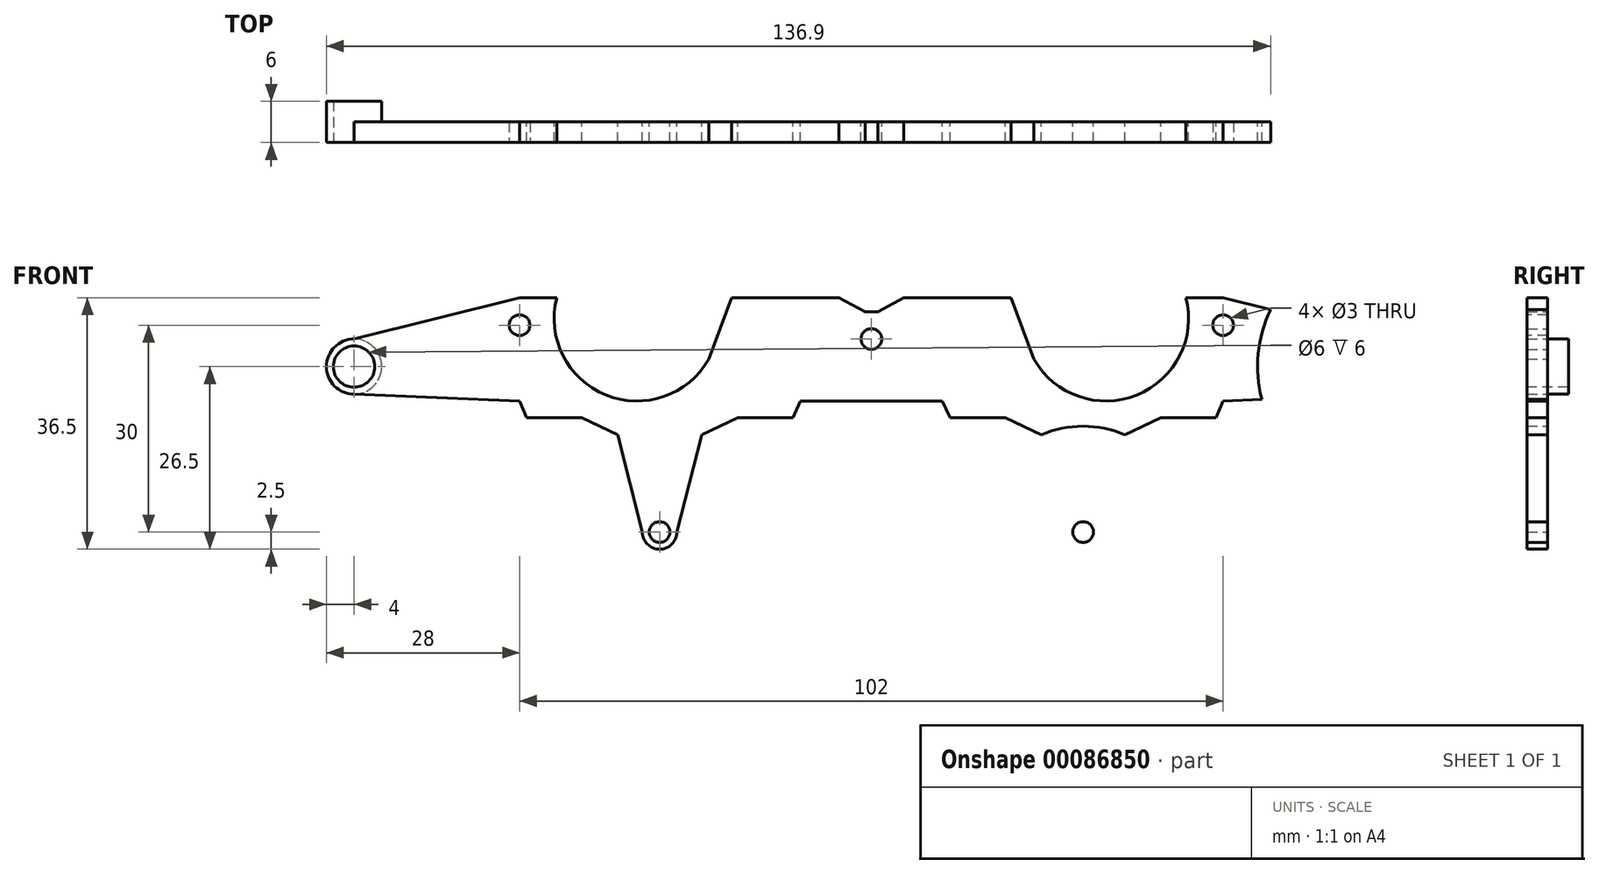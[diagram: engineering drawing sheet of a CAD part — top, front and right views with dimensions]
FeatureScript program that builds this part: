
annotation { "Feature Type Name" : "Feature", "Feature Type Description" : "" }
export const myFeature = defineFeature(function(context is Context, id is Id, definition is map)
    precondition{}
    {
        {
            var Q0;
            Q0=qCreatedBy(makeId("Front.planeOp"),FACE);
            var sketch = newSketch(context, id + "F0", { "sketchPlane" : qUnion([Q0])});
            skCircle(sketch, "E0", {"center": v(-75, 14) * mm, "radius": 16 * mm, "construction": true});
            skCircle(sketch, "E1", {"center": v(-46, -16) * mm, "radius": 9 * mm, "construction": true});
            skCircle(sketch, "E2", {"center": v(-15.4, -16) * mm, "radius": 9 * mm, "construction": true});
            skCircle(sketch, "E3", {"center": v(-34, 21) * mm, "radius": 9 * mm, "construction": true});
            skLineSegment(sketch, "E4", {"start": v(-75, 14) * mm, "end": v(75, 14) * mm, "construction": true});
            skLineSegment(sketch, "E5", {"start": v(-30.7, 14) * mm, "end": v(-30.7, -10) * mm, "construction": true});
            skArc(sketch, "E6", {"start": v(-75, 18) * mm, "mid": v(-79, 14) * mm, "end": v(-75, 10) * mm});
            skLineSegment(sketch, "E7", {"start": v(-51, 9) * mm, "end": v(-51, 24) * mm, "construction": true});
            skLineSegment(sketch, "E8", {"start": v(-75, 18) * mm, "end": v(-51, 24) * mm});
            skLineSegment(sketch, "E9", {"start": v(-51, 9) * mm, "end": v(-75, 10) * mm});
            skArc(sketch, "E10", {"start": v(-33.2, -10) * mm, "mid": v(-30.7, -12.5) * mm, "end": v(-28.2, -10) * mm});
            skLineSegment(sketch, "E11", {"start": v(-34, 21) * mm, "end": v(0, 18) * mm, "construction": true});
            skLineSegment(sketch, "E12", {"start": v(-51, 24) * mm, "end": v(-45.62, 24) * mm});
            skArc(sketch, "E13", {"start": v(-45.62, 24) * mm, "mid": v(-38.5, 9.88) * mm, "end": v(-23.57, 15.06) * mm});
            skLineSegment(sketch, "E14", {"start": v(-46, -16) * mm, "end": v(-30.7, -10) * mm, "construction": true});
            skLineSegment(sketch, "E15", {"start": v(-15.4, -16) * mm, "end": v(-30.7, -10) * mm, "construction": true});
            skLineSegment(sketch, "E16", {"start": v(-4.7, 24) * mm, "end": v(0, 24) * mm});
            skLineSegment(sketch, "E17", {"start": v(0, 18) * mm, "end": v(-29.94, 34.4) * mm, "construction": true});
            skCircle(sketch, "E18", {"center": v(-75, 14) * mm, "radius": 4 * mm});
            skCircle(sketch, "E19", {"center": v(-29.94, 34.4) * mm, "radius": 9 * mm, "construction": true});
            skArc(sketch, "E20", {"start": v(-56.6, 9.23) * mm, "mid": v(-56.1, 15.87) * mm, "end": v(-57.9, 22.28) * mm});
            skLineSegment(sketch, "E21", {"start": v(0, 24) * mm, "end": v(0, 24) * mm});
            skCircle(sketch, "E22", {"center": v(-30.7, -10) * mm, "radius": 1.5 * mm});
            skLineSegment(sketch, "E23", {"start": v(-24.6, 4.1) * mm, "end": v(-19.4, 6.6) * mm});
            skLineSegment(sketch, "E24", {"start": v(-36.8, 4.1) * mm, "end": v(-42, 6.6) * mm});
            skArc(sketch, "E25", {"start": v(-24.6, 4.1) * mm, "mid": v(-30.7, 5.35) * mm, "end": v(-36.8, 4.1) * mm});
            skLineSegment(sketch, "E26", {"start": v(-23.57, 15.06) * mm, "end": v(0, 12.98) * mm});
            skCircle(sketch, "E27", {"center": v(-75, 14) * mm, "radius": 3 * mm});
            skLineSegment(sketch, "E28", {"start": v(-28.2, -10) * mm, "end": v(-24.6, 4.1) * mm});
            skLineSegment(sketch, "E29", {"start": v(-36.8, 4.1) * mm, "end": v(-33.2, -10) * mm});
            skLineSegment(sketch, "E30", {"start": v(-11.4, 6.6) * mm, "end": v(-19.4, 6.6) * mm});
            skLineSegment(sketch, "E31", {"start": v(-42, 6.6) * mm, "end": v(-50, 6.6) * mm});
            skLineSegment(sketch, "E32", {"start": v(-50, 6.6) * mm, "end": v(-51, 9) * mm});
            skLineSegment(sketch, "E33", {"start": v(-4.7, 24) * mm, "end": v(-0.92, 21.92) * mm});
            skPoint(sketch, "E34", {"position": v(-46, 6.6) * mm});
            skPoint(sketch, "E35", {"position": v(-15.4, 6.6) * mm});
            skLineSegment(sketch, "E36", {"start": v(-11.4, 6.6) * mm, "end": v(-10.28, 9) * mm});
            skLineSegment(sketch, "E37", {"start": v(-4.7, 24) * mm, "end": v(-20.26, 24) * mm});
            skArc(sketch, "E38", {"start": v(-22.04, 30.08) * mm, "mid": v(-24.05, 25.3) * mm, "end": v(-25.04, 20.2) * mm, "construction": true});
            skCircle(sketch, "E39.MirrorC", {"center": v(30.7, -10) * mm, "radius": 1.5 * mm});
            skLineSegment(sketch, "E40.MirrorCS", {"start": v(4.7, 24) * mm, "end": v(0, 24) * mm});
            skLineSegment(sketch, "E41.MirrorCS", {"start": v(4.7, 24) * mm, "end": v(0.92, 21.92) * mm});
            skLineSegment(sketch, "E42.MirrorCS", {"start": v(50, 6.6) * mm, "end": v(51, 9) * mm});
            skArc(sketch, "E43.MirrorCS", {"start": v(33.2, -10) * mm, "mid": v(30.7, -12.5) * mm, "end": v(28.2, -10) * mm});
            skLineSegment(sketch, "E44.MirrorCS", {"start": v(11.4, 6.6) * mm, "end": v(10.28, 9) * mm});
            skLineSegment(sketch, "E45.MirrorCS", {"start": v(28.2, -10) * mm, "end": v(24.6, 4.1) * mm});
            skLineSegment(sketch, "E46.MirrorCS", {"start": v(36.8, 4.1) * mm, "end": v(33.2, -10) * mm});
            skLineSegment(sketch, "E47.MirrorCS", {"start": v(42, 6.6) * mm, "end": v(50, 6.6) * mm});
            skArc(sketch, "E48.MirrorCS", {"start": v(22.04, 30.08) * mm, "mid": v(24.05, 25.3) * mm, "end": v(25.04, 20.2) * mm, "construction": true});
            skLineSegment(sketch, "E49.MirrorCS", {"start": v(19.4, 6.6) * mm, "end": v(11.4, 6.6) * mm});
            skLineSegment(sketch, "E50.MirrorCS", {"start": v(24.6, 4.1) * mm, "end": v(19.4, 6.6) * mm});
            skCircle(sketch, "E51.MirrorC", {"center": v(75, 14) * mm, "radius": 16 * mm, "construction": true});
            skCircle(sketch, "E52.MirrorC", {"center": v(29.94, 34.4) * mm, "radius": 9 * mm, "construction": true});
            skCircle(sketch, "E53.MirrorC", {"center": v(15.4, -16) * mm, "radius": 9 * mm, "construction": true});
            skLineSegment(sketch, "E54.MirrorCS", {"start": v(15.4, -16) * mm, "end": v(30.7, -10) * mm, "construction": true});
            skLineSegment(sketch, "E55.MirrorCS", {"start": v(36.8, 4.1) * mm, "end": v(42, 6.6) * mm});
            skLineSegment(sketch, "E56.MirrorCS", {"start": v(30.7, 14) * mm, "end": v(30.7, -10) * mm, "construction": true});
            skArc(sketch, "E57.MirrorCS", {"start": v(56.6, 9.23) * mm, "mid": v(56.1, 15.87) * mm, "end": v(57.9, 22.28) * mm});
            skArc(sketch, "E58.MirrorCS", {"start": v(45.62, 24) * mm, "mid": v(38.5, 9.88) * mm, "end": v(23.57, 15.06) * mm});
            skCircle(sketch, "E59.MirrorC", {"center": v(46, -16) * mm, "radius": 9 * mm, "construction": true});
            skCircle(sketch, "E60.MirrorC", {"center": v(75, 14) * mm, "radius": 1.5 * mm});
            skArc(sketch, "E61.MirrorCS", {"start": v(24.6, 4.1) * mm, "mid": v(30.7, 5.35) * mm, "end": v(36.8, 4.1) * mm});
            skLineSegment(sketch, "E62.MirrorCS", {"start": v(51, 9) * mm, "end": v(51, 24) * mm, "construction": true});
            skPoint(sketch, "E63.MirrorP", {"position": v(46, 6.6) * mm});
            skCircle(sketch, "E64.MirrorC", {"center": v(34, 21) * mm, "radius": 9 * mm, "construction": true});
            skPoint(sketch, "E65.MirrorP", {"position": v(15.4, 6.6) * mm});
            skLineSegment(sketch, "E66.MirrorCS", {"start": v(0, 18) * mm, "end": v(29.94, 34.4) * mm, "construction": true});
            skLineSegment(sketch, "E67.MirrorCS", {"start": v(51, 24) * mm, "end": v(45.62, 24) * mm});
            skLineSegment(sketch, "E68.MirrorCS", {"start": v(23.57, 15.06) * mm, "end": v(0, 12.98) * mm});
            skLineSegment(sketch, "E69.MirrorCS", {"start": v(4.7, 24) * mm, "end": v(20.26, 24) * mm});
            skLineSegment(sketch, "E70.MirrorCS", {"start": v(51, 9) * mm, "end": v(56.6, 9.23) * mm});
            skLineSegment(sketch, "E71.MirrorCS", {"start": v(34, 21) * mm, "end": v(0, 18) * mm, "construction": true});
            skLineSegment(sketch, "E72.MirrorCS", {"start": v(46, -16) * mm, "end": v(30.7, -10) * mm, "construction": true});
            skLineSegment(sketch, "E73", {"start": v(-10.28, 9) * mm, "end": v(10.28, 9) * mm});
            skCircle(sketch, "E74", {"center": v(0, 18) * mm, "radius": 1.5 * mm});
            skLineSegment(sketch, "E75", {"start": v(51, 24) * mm, "end": v(57.9, 22.28) * mm});
            skLineSegment(sketch, "E76", {"start": v(57.9, 22.28) * mm, "end": v(73.57, 21.87) * mm});
            skLineSegment(sketch, "E77", {"start": v(73.57, 21.87) * mm, "end": v(83, 21.87) * mm});
            skLineSegment(sketch, "E78", {"start": v(56.6, 9.23) * mm, "end": v(83, 9.23) * mm});
            skLineSegment(sketch, "E79", {"start": v(83, 9.23) * mm, "end": v(83, 21.87) * mm});
            skLineSegment(sketch, "E80", {"start": v(-0.92, 21.92) * mm, "end": v(0.92, 21.92) * mm});
            skLineSegment(sketch, "E81", {"start": v(-20.26, 24) * mm, "end": v(-23.57, 15.06) * mm});
            skLineSegment(sketch, "E82", {"start": v(20.26, 24) * mm, "end": v(23.57, 15.06) * mm});
            skSolve(sketch);
        }
        {
            var Q0;
            {var subQ3=sQuery(id+"F0.wireOp",EDGE,"E20");Q0=makeQuery(id+"F0.imprint","IMPRINT",FACE,{"disambiguationData":[TD([[makeQuery(id+"F0.imprint","IMPRINT",EDGE,{"derivedFrom":subQ3}),1.0]])]});}
            var Q1;
            {var subQ4=sQuery(id+"F0.wireOp",EDGE,"E12");Q1=makeQuery(id+"F0.imprint","IMPRINT",FACE,{"disambiguationData":[TD([[makeQuery(id+"F0.imprint","IMPRINT",EDGE,{"derivedFrom":subQ4}),-1.0]])]});}
            var Q2;
            Q2=makeQuery(id+"F0.imprint","IMPRINT",FACE,{"disambiguationData":[TD([[makeQuery(id+"F0.imprint","IMPRINT",EDGE,{"derivedFrom":sQuery(id+"F0.wireOp",EDGE,"E26")}),1.0]])]});
            var Q3;
            {var subQ1=sQuery(id+"F0.wireOp",EDGE,"E57.MirrorCS");Q3=makeQuery(id+"F0.imprint","IMPRINT",FACE,{"disambiguationData":[TD([[makeQuery(id+"F0.imprint","IMPRINT",EDGE,{"derivedFrom":subQ1}),-1.0]])]});}
            var Q4;
            Q4=makeQuery(id+"F0.imprint","IMPRINT",FACE,{"disambiguationData":[TD([[makeQuery(id+"F0.imprint","IMPRINT",EDGE,{"derivedFrom":sQuery(id+"F0.wireOp",EDGE,"E39.MirrorC")}),1.0]])]});
            var Q5;
            Q5=makeQuery(id+"F0.imprint","IMPRINT",FACE,{"disambiguationData":[TD([[makeQuery(id+"F0.imprint","IMPRINT",EDGE,{"derivedFrom":sQuery(id+"F0.wireOp",EDGE,"E10")}),1.0]])]});
            extrude(context, id + "F1", {"entities" : qUnion([Q0, Q1, Q2, Q3, Q4, Q5]), "depth" : 3 * mm});
        }
        {
            var Q0;
            Q0=makeQuery(id+"F0.imprint","IMPRINT",FACE,{"disambiguationData":[TD([[makeQuery(id+"F0.imprint","IMPRINT",EDGE,{"derivedFrom":sQuery(id+"F0.wireOp",EDGE,"E27")}),-1.0]])]});
            extrude(context, id + "F2", {"entities" : qUnion([Q0]), "operationType" : NewBodyOperationType.ADD, "oppositeDirection" : true, "depth" : (2 * 2.5 + 1) * mm, "symmetric" : true});
        }
        {
            var Q0;
            {var subQ0=sQuery(id+"F0.wireOp",EDGE,"E18");Q0=makeQuery(id+"F2.boolean.opBoolean","MERGE",FACE,{"derivedFrom":[makeQuery(id+"F1.opExtrude","CAP_FACE",FACE,{"disambiguationData":[OSD([sQuery(id+"F0.wireOp",EDGE,"E8"),sQuery(id+"F0.wireOp",EDGE,"E9"),sQuery(id+"F0.wireOp",EDGE,"E10"),sQuery(id+"F0.wireOp",EDGE,"E12"),sQuery(id+"F0.wireOp",EDGE,"E13"),subQ0,sQuery(id+"F0.wireOp",EDGE,"E22"),sQuery(id+"F0.wireOp",EDGE,"E23"),sQuery(id+"F0.wireOp",EDGE,"E24"),sQuery(id+"F0.wireOp",EDGE,"E28"),sQuery(id+"F0.wireOp",EDGE,"E29"),sQuery(id+"F0.wireOp",EDGE,"E30"),sQuery(id+"F0.wireOp",EDGE,"E31"),sQuery(id+"F0.wireOp",EDGE,"E32"),sQuery(id+"F0.wireOp",EDGE,"E33"),sQuery(id+"F0.wireOp",EDGE,"E36"),sQuery(id+"F0.wireOp",EDGE,"E37"),sQuery(id+"F0.wireOp",EDGE,"E39.MirrorC"),sQuery(id+"F0.wireOp",EDGE,"E41.MirrorCS"),sQuery(id+"F0.wireOp",EDGE,"E42.MirrorCS"),sQuery(id+"F0.wireOp",EDGE,"E43.MirrorCS"),sQuery(id+"F0.wireOp",EDGE,"E44.MirrorCS"),sQuery(id+"F0.wireOp",EDGE,"E45.MirrorCS"),sQuery(id+"F0.wireOp",EDGE,"E46.MirrorCS"),sQuery(id+"F0.wireOp",EDGE,"E47.MirrorCS"),sQuery(id+"F0.wireOp",EDGE,"E49.MirrorCS"),sQuery(id+"F0.wireOp",EDGE,"E50.MirrorCS"),sQuery(id+"F0.wireOp",EDGE,"E55.MirrorCS"),sQuery(id+"F0.wireOp",EDGE,"E58.MirrorCS"),sQuery(id+"F0.wireOp",EDGE,"E60.MirrorC"),sQuery(id+"F0.wireOp",EDGE,"E67.MirrorCS"),sQuery(id+"F0.wireOp",EDGE,"E69.MirrorCS"),sQuery(id+"F0.wireOp",EDGE,"E70.MirrorCS"),sQuery(id+"F0.wireOp",EDGE,"E73"),sQuery(id+"F0.wireOp",EDGE,"E74"),sQuery(id+"F0.wireOp",EDGE,"E75"),sQuery(id+"F0.wireOp",EDGE,"E76"),sQuery(id+"F0.wireOp",EDGE,"E77"),sQuery(id+"F0.wireOp",EDGE,"E78"),sQuery(id+"F0.wireOp",EDGE,"E79"),sQuery(id+"F0.wireOp",EDGE,"E80"),sQuery(id+"F0.wireOp",EDGE,"E81"),sQuery(id+"F0.wireOp",EDGE,"E82")])],"isStart":false}),makeQuery(id+"F2.opExtrude","CAP_FACE",FACE,{"disambiguationData":[OSD([subQ0,sQuery(id+"F0.wireOp",EDGE,"E27")])],"isStart":true})]});}
            var sketch = newSketch(context, id + "F3", { "sketchPlane" : qUnion([Q0])});
            skLineSegment(sketch, "E83", {"start": v(-51, 24) * mm, "end": v(-51, 20) * mm, "construction": true});
            skLineSegment(sketch, "E84", {"start": v(51, 24) * mm, "end": v(51, 20) * mm, "construction": true});
            skSolve(sketch);
        }
        {
            var Q0;
            Q0=sQuery(id+"F3.wireOp",VERTEX,"E83.end");
            var Q1;
            Q1=sQuery(id+"F3.wireOp",VERTEX,"E84.end");
            var Q2;
            Q2=makeQuery(id+"F1.opExtrude","SWEPT_BODY",BODY,{"disambiguationData":[OSD([sQuery(id+"F0.wireOp",EDGE,"E8"),sQuery(id+"F0.wireOp",EDGE,"E9"),sQuery(id+"F0.wireOp",EDGE,"E10"),sQuery(id+"F0.wireOp",EDGE,"E12"),sQuery(id+"F0.wireOp",EDGE,"E13"),sQuery(id+"F0.wireOp",EDGE,"E18"),sQuery(id+"F0.wireOp",EDGE,"E22"),sQuery(id+"F0.wireOp",EDGE,"E23"),sQuery(id+"F0.wireOp",EDGE,"E24"),sQuery(id+"F0.wireOp",EDGE,"E28"),sQuery(id+"F0.wireOp",EDGE,"E29"),sQuery(id+"F0.wireOp",EDGE,"E30"),sQuery(id+"F0.wireOp",EDGE,"E31"),sQuery(id+"F0.wireOp",EDGE,"E32"),sQuery(id+"F0.wireOp",EDGE,"E33"),sQuery(id+"F0.wireOp",EDGE,"E36"),sQuery(id+"F0.wireOp",EDGE,"E37"),sQuery(id+"F0.wireOp",EDGE,"E39.MirrorC"),sQuery(id+"F0.wireOp",EDGE,"E41.MirrorCS"),sQuery(id+"F0.wireOp",EDGE,"E42.MirrorCS"),sQuery(id+"F0.wireOp",EDGE,"E43.MirrorCS"),sQuery(id+"F0.wireOp",EDGE,"E44.MirrorCS"),sQuery(id+"F0.wireOp",EDGE,"E45.MirrorCS"),sQuery(id+"F0.wireOp",EDGE,"E46.MirrorCS"),sQuery(id+"F0.wireOp",EDGE,"E47.MirrorCS"),sQuery(id+"F0.wireOp",EDGE,"E49.MirrorCS"),sQuery(id+"F0.wireOp",EDGE,"E50.MirrorCS"),sQuery(id+"F0.wireOp",EDGE,"E55.MirrorCS"),sQuery(id+"F0.wireOp",EDGE,"E58.MirrorCS"),sQuery(id+"F0.wireOp",EDGE,"E60.MirrorC"),sQuery(id+"F0.wireOp",EDGE,"E67.MirrorCS"),sQuery(id+"F0.wireOp",EDGE,"E69.MirrorCS"),sQuery(id+"F0.wireOp",EDGE,"E70.MirrorCS"),sQuery(id+"F0.wireOp",EDGE,"E73"),sQuery(id+"F0.wireOp",EDGE,"E74"),sQuery(id+"F0.wireOp",EDGE,"E75"),sQuery(id+"F0.wireOp",EDGE,"E76"),sQuery(id+"F0.wireOp",EDGE,"E77"),sQuery(id+"F0.wireOp",EDGE,"E78"),sQuery(id+"F0.wireOp",EDGE,"E79"),sQuery(id+"F0.wireOp",EDGE,"E80"),sQuery(id+"F0.wireOp",EDGE,"E81"),sQuery(id+"F0.wireOp",EDGE,"E82")])]});
            hole(context, id + "F4", {"style" : HoleStyle.SIMPLE, "endStyle" : HoleEndStyle.THROUGH, "holeDiameter" : 3 * mm, "locations" : qUnion([Q0, Q1]), "scope" : qUnion([Q2]), "isTappedThrough" : true});
        }
    });
